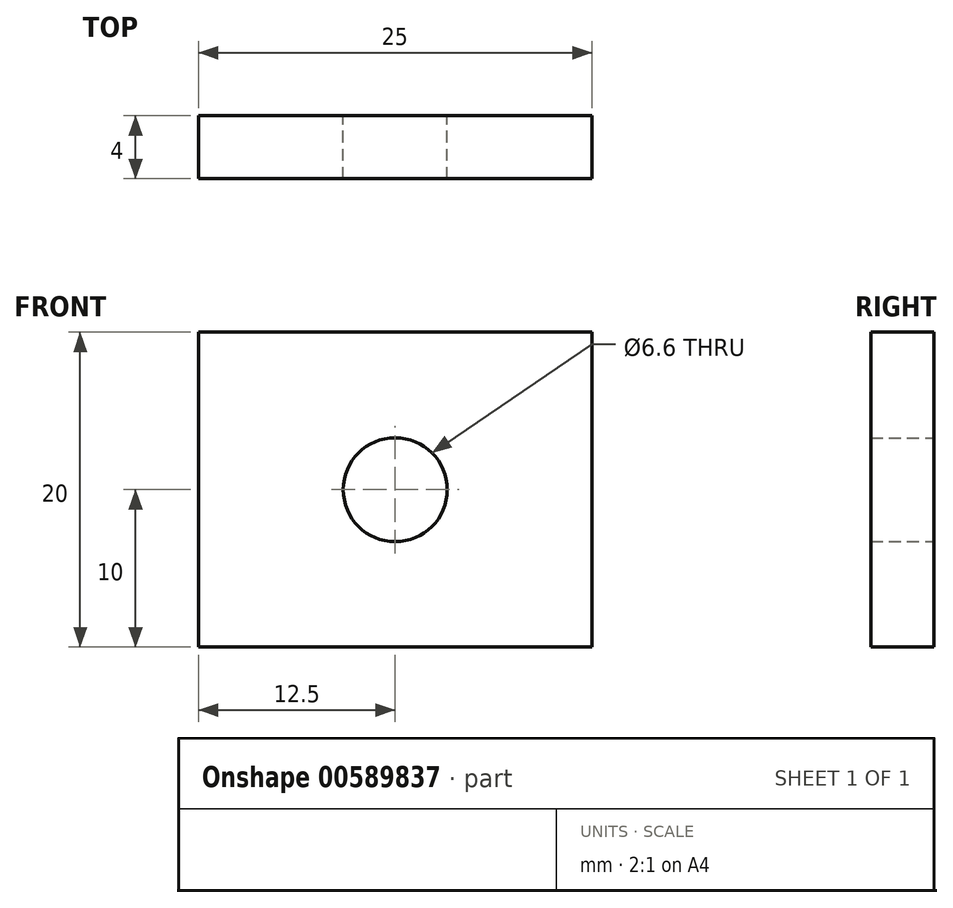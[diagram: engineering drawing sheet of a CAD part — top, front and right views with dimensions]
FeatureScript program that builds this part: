
annotation { "Feature Type Name" : "Feature", "Feature Type Description" : "" }
export const myFeature = defineFeature(function(context is Context, id is Id, definition is map)
    precondition{}
    {
        {
            var Q0;
            Q0=qCreatedBy(makeId("Front.planeOp"),FACE);
            var sketch = newSketch(context, id + "F0", { "sketchPlane" : qUnion([Q0])});
            skLineSegment(sketch, "E0.bottom", {"start": v(12.5, 10) * mm, "end": v(-12.5, 10) * mm});
            skLineSegment(sketch, "E0.top", {"start": v(12.5, -10) * mm, "end": v(-12.5, -10) * mm});
            skLineSegment(sketch, "E0.left", {"start": v(12.5, 10) * mm, "end": v(12.5, -10) * mm});
            skLineSegment(sketch, "E0.right", {"start": v(-12.5, 10) * mm, "end": v(-12.5, -10) * mm});
            skPoint(sketch, "E0.middle", {"position": v(0, 0) * mm});
            skCircle(sketch, "E1", {"center": v(0, 0) * mm, "radius": 3.3 * mm});
            skSolve(sketch);
        }
        {
            var Q0;
            Q0=makeQuery(id+"F0.imprint","IMPRINT",FACE,{"disambiguationData":[TD([[makeQuery(id+"F0.imprint","IMPRINT",EDGE,{"derivedFrom":sQuery(id+"F0.wireOp",EDGE,"E0.bottom")}),1.0]])]});
            extrude(context, id + "F1", {"entities" : qUnion([Q0]), "depth" : 4 * mm, "offsetDistance" : 25 * mm});
        }
    });
